# Revit family: Spout-Grohe-Defined-26637_Series
name_source: partatom
category: Plumbing Fixtures
units: mm (PartAtom-declared; Revit-internal decimal feet)

## family parameters
Cut with Voids When Loaded = No
Host = Face
OmniClass Number = 23.45.05.14.21.11
OmniClass Title = Bath/Shower Units
Part Type = Normal
Room Calculation Point = No
Round Connector Dimension = Use Diameter
Shared = Yes

## types (2) — shared parameters
Assembly Code = D2020300
CW Connection = No
CWFU = 3
Default Elevation = 21"
HW Connection = No
HWFU = 3
Height = 3 3/16"
Installation Type = Wall Mounted
Length = 7 7/8"
Manufacturer = Grohe
Product Documentation Link = https://americanstandard.box.com
Product Page URL = https://www.grohe.us
Revised Date = 06/06/2023
Tempered Connection Diameter = 1/2"
Tempered Connection Radius = 1/4"
Tempered Water Connection = Yes
URL = https://www.grohe.us
Vent Connection = No
WFU = 4
Warranty Information = Limited lifetime warranty
Waste Connection = No
Width = 3 1/8"

## per-type parameters (varying)
| type | Description | Finish | Material |
| 26637000 | DEFINED Diverter Tub Spout Starlight Chrome | Brass-Grohe-000-Starlight Chrome | Brass-Grohe-000-Starlight Chrome |
| 26637EN0 | DEFINED Diverter Tub Spout Brushed Nickel | Brass-Grohe-EN0-Brushed Nickel | Brass-Grohe-EN0-Brushed Nickel |

note: column(s) folded — value = type name in every type: Model

## geometry (parser evidence)
native form markers: Sweep x3
no freeform markers — native parametric forms only
